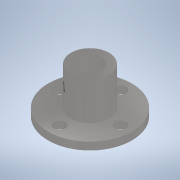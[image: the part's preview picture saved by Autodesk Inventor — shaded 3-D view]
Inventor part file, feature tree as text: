
AUTODESK INVENTOR PART (.ipt)
format: ipt  version: 2020.2 (Build 242310000, 310)  size: 218,624 bytes
history: native  units: mm
features: sketch x7, extrude x5, hole x2
ambient origin geometry x8: Origin, YZ Plane, XZ Plane, XY Plane, X Axis, Y Axis, Z Axis, Center Point
bodies: Solido1 (feature_tree)
feature tree (14):
  extrude  "Estrusione1"  Depth=22.0mm
  extrude  "Estrusione2"  Depth=2.0mm TaperAngle=0.0deg
  extrude  "Estrusione3"  Depth=10.0mm
  extrude  "Estrusione4"  Depth=10.0mm TaperAngle=0.0deg
  hole  "Foro1"  [1 undecoded]
  sketch  "Schizzo7"
  hole  "Foro2"  [1 undecoded]
  extrude  "Estrusione5"  Depth=16.0mm
  sketch  "Schizzo1"
  sketch  "Schizzo2"
  sketch  "Schizzo3"
  sketch  "Schizzo4"
  sketch  "Schizzo5"
  sketch  "Schizzo6"
note: 2 required parameter values undecoded (feature->parameter linkage not recoverable at this tier; creation-order binding heuristic only, values carry confidence <= 0.55)
